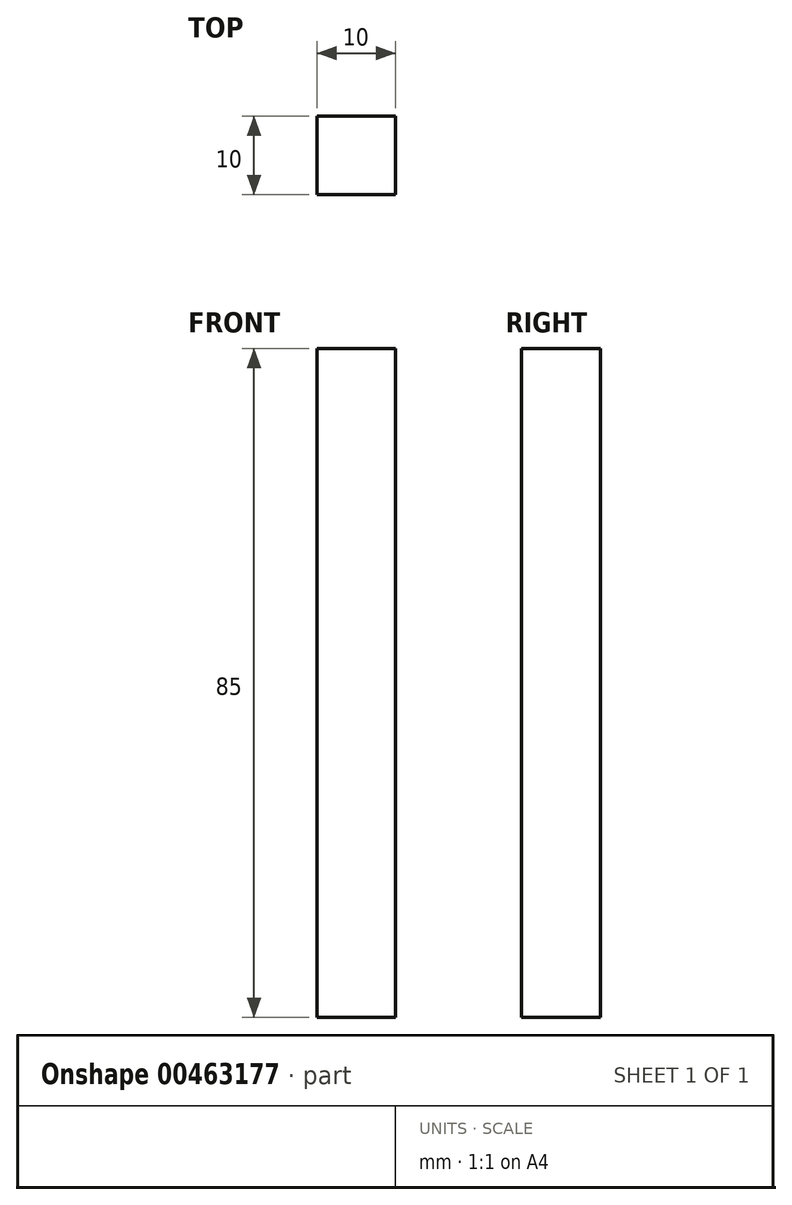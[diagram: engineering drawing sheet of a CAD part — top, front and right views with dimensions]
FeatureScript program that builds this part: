
annotation { "Feature Type Name" : "Feature", "Feature Type Description" : "" }
export const myFeature = defineFeature(function(context is Context, id is Id, definition is map)
    precondition{}
    {
        {
            var Q0;
            Q0=qCreatedBy(makeId("Front.planeOp"),FACE);
            var sketch = newSketch(context, id + "F0", { "sketchPlane" : qUnion([Q0])});
            skLineSegment(sketch, "E0.bottom", {"start": v(10, 85) * mm, "end": v(0, 85) * mm});
            skLineSegment(sketch, "E0.top", {"start": v(10, 0) * mm, "end": v(0, 0) * mm});
            skLineSegment(sketch, "E0.left", {"start": v(10, 85) * mm, "end": v(10, 0) * mm});
            skLineSegment(sketch, "E0.right", {"start": v(0, 85) * mm, "end": v(0, 0) * mm});
            skSolve(sketch);
        }
        {
            var Q0;
            Q0=makeQuery(id+"F0.imprint","IMPRINT",FACE,{"disambiguationData":[TD([[makeQuery(id+"F0.imprint","IMPRINT",EDGE,{"derivedFrom":sQuery(id+"F0.wireOp",EDGE,"E0.bottom")}),1.0]])]});
            extrude(context, id + "F1", {"entities" : qUnion([Q0]), "depth" : 10 * mm});
        }
    });
